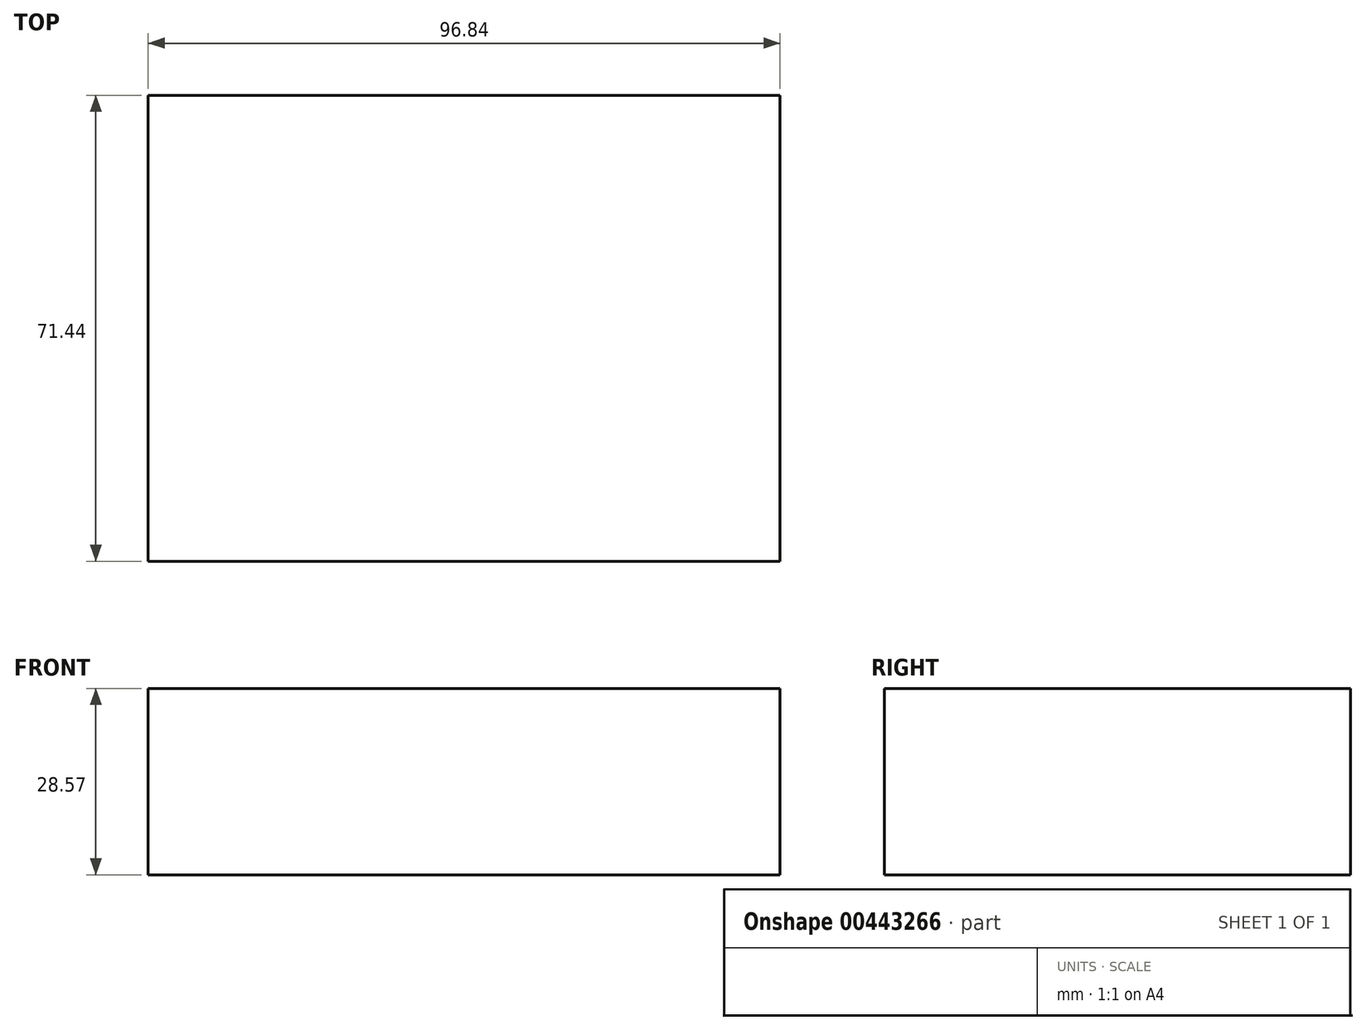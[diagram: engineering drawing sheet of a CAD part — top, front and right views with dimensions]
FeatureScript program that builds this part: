
annotation { "Feature Type Name" : "Feature", "Feature Type Description" : "" }
export const myFeature = defineFeature(function(context is Context, id is Id, definition is map)
    precondition{}
    {
        {
            var Q0;
            Q0=qCreatedBy(makeId("Top.planeOp"),FACE);
            var sketch = newSketch(context, id + "F0", { "sketchPlane" : qUnion([Q0])});
            skLineSegment(sketch, "E0.bottom", {"start": v(0, 0) * mm, "end": v(96.84, 0) * mm});
            skLineSegment(sketch, "E0.top", {"start": v(0, 71.44) * mm, "end": v(96.84, 71.44) * mm});
            skLineSegment(sketch, "E0.left", {"start": v(0, 0) * mm, "end": v(0, 71.44) * mm});
            skLineSegment(sketch, "E0.right", {"start": v(96.84, 0) * mm, "end": v(96.84, 71.44) * mm});
            skSolve(sketch);
        }
        {
            var Q0;
            Q0 = qSketchRegion(id + "F0", true);
            extrude(context, id + "F1", {"entities" : qUnion([Q0]), "depth" : 28.57 * mm});
        }
    });
